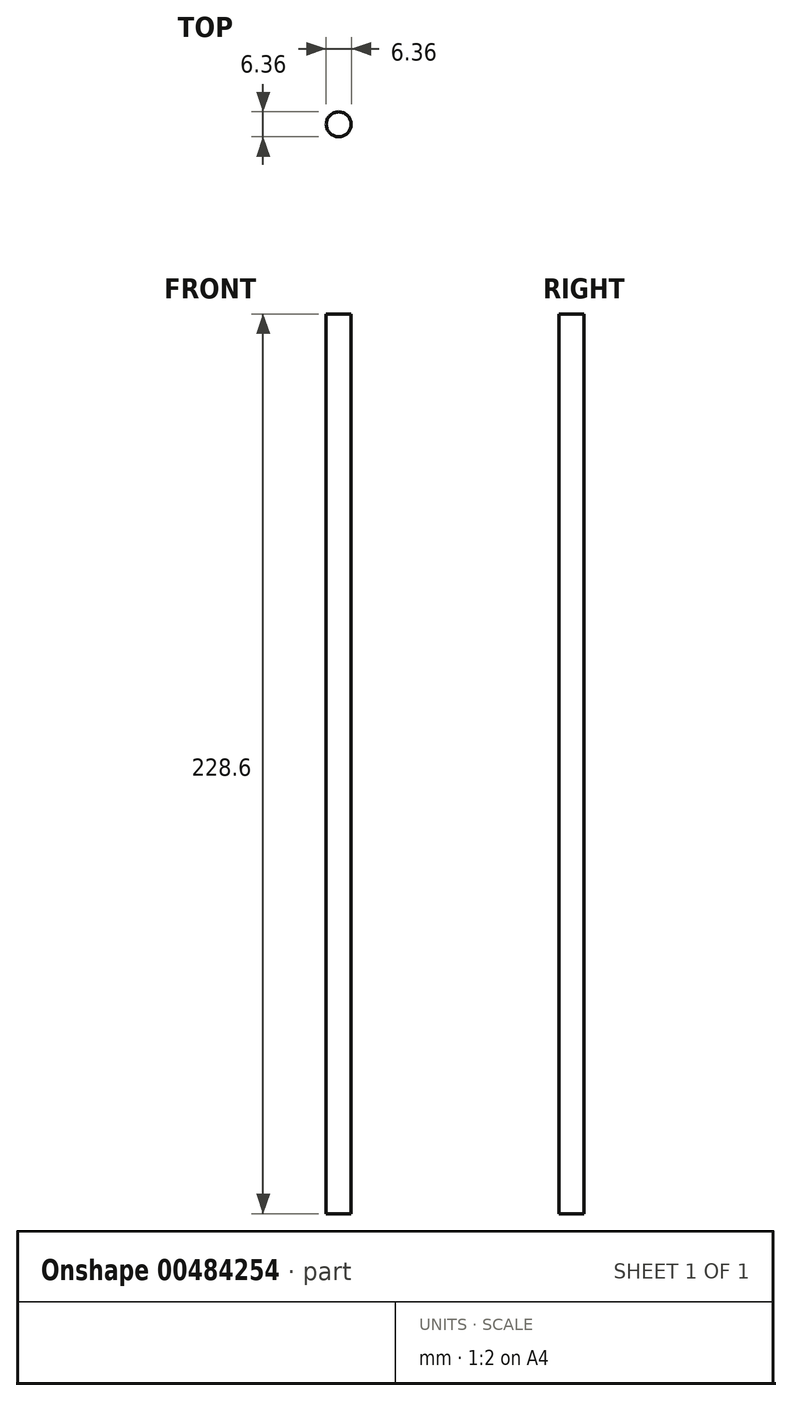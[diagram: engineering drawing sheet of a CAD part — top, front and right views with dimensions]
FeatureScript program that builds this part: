
annotation { "Feature Type Name" : "Feature", "Feature Type Description" : "" }
export const myFeature = defineFeature(function(context is Context, id is Id, definition is map)
    precondition{}
    {
        {
            var Q0;
            Q0=qCreatedBy(makeId("Top.planeOp"),FACE);
            var sketch = newSketch(context, id + "F0", { "sketchPlane" : qUnion([Q0])});
            skCircle(sketch, "E0", {"center": v(0, 0) * mm, "radius": 3.18 * mm});
            skSolve(sketch);
        }
        {
            var Q0;
            Q0 = qSketchRegion(id + "F0", true);
            extrude(context, id + "F1", {"entities" : qUnion([Q0]), "depth" : 228.6 * mm});
        }
    });
